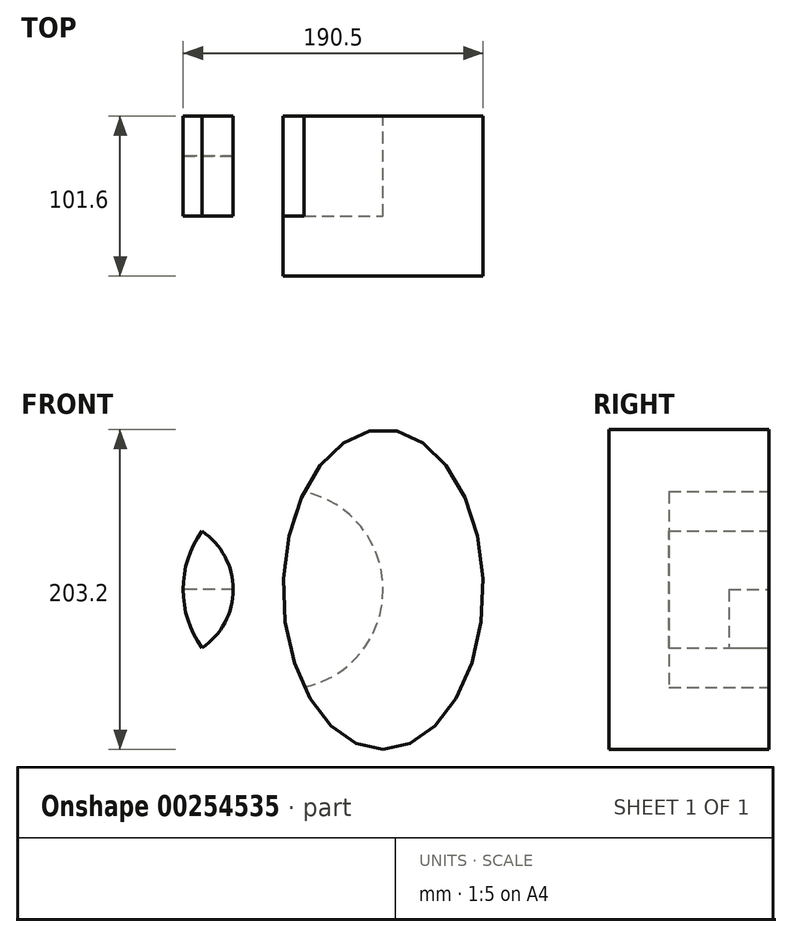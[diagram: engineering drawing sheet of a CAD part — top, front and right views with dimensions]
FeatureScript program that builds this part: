
annotation { "Feature Type Name" : "Feature", "Feature Type Description" : "" }
export const myFeature = defineFeature(function(context is Context, id is Id, definition is map)
    precondition{}
    {
        {
            var Q0;
            Q0=qCreatedBy(makeId("Front.planeOp"),FACE);
            var sketch = newSketch(context, id + "F0", { "sketchPlane" : qUnion([Q0])});
            skLineSegment(sketch, "E0", {"start": v(0, 0) * mm, "end": v(-76.2, 0) * mm});
            skCircle(sketch, "E1", {"center": v(-76.2, 0) * mm, "radius": 44.45 * mm});
            skLineSegment(sketch, "E2", {"start": v(-31.75, 0) * mm, "end": v(-63.5, 0) * mm});
            skCircle(sketch, "E3", {"center": v(0, 0) * mm, "radius": 63.5 * mm});
            skLineSegment(sketch, "E4", {"start": v(63.5, 0) * mm, "end": v(63.5, 101.6) * mm});
            skEllipse(sketch, "E5", {"center": v(63.5, 0) * mm, "majorRadius": 63.5 * mm, "minorRadius": 101.6 * mm, "majorAxis": v(-1, 0)});
            skSolve(sketch);
        }
        {
            var Q0;
            {var subQ0=sQuery(id+"F0.wireOp",EDGE,"E3");var subQ1=sQuery(id+"F0.wireOp",EDGE,"E1");var subQ2=makeQuery(id+"F0.imprint","INTERSECT",VERTEX,{"disambiguationData":[OD(0.0)],"derivedFrom":[subQ1,subQ0]});Q0=makeQuery(id+"F0.imprint","IMPRINT",FACE,{"disambiguationData":[TD([[makeQuery(id+"F0.imprint","IMPRINT",EDGE,{"disambiguationData":[TD([[subQ2,-1.0]])],"derivedFrom":subQ1}),1.0]])]});}
            extrude(context, id + "F1", {"entities" : qUnion([Q0]), "depth" : 25.4 * mm});
        }
        {
            var Q0;
            {var subQ3=sQuery(id+"F0.wireOp",EDGE,"E1");var subQ5=sQuery(id+"F0.wireOp",EDGE,"E3");var subQ6=makeQuery(id+"F0.imprint","INTERSECT",VERTEX,{"disambiguationData":[OD(0.0)],"derivedFrom":[subQ3,subQ5]});Q0=makeQuery(id+"F0.imprint","IMPRINT",FACE,{"disambiguationData":[TD([[makeQuery(id+"F0.imprint","IMPRINT",EDGE,{"disambiguationData":[TD([[subQ6,1.0]])],"derivedFrom":subQ5}),1.0]])]});}
            var Q1;
            {var subQ0=sQuery(id+"F0.wireOp",EDGE,"E2");Q1=makeQuery(id+"F0.imprint","IMPRINT",FACE,{"disambiguationData":[TD([[makeQuery(id+"F0.imprint","IMPRINT",EDGE,{"derivedFrom":subQ0}),-1.0]])]});}
            var Q2;
            {var subQ3=sQuery(id+"F0.wireOp",EDGE,"E1");var subQ5=sQuery(id+"F0.wireOp",EDGE,"E3");var subQ6=makeQuery(id+"F0.imprint","INTERSECT",VERTEX,{"disambiguationData":[OD(1.0)],"derivedFrom":[subQ3,subQ5]});Q2=makeQuery(id+"F0.imprint","IMPRINT",FACE,{"disambiguationData":[TD([[makeQuery(id+"F0.imprint","IMPRINT",EDGE,{"disambiguationData":[TD([[subQ6,-1.0]])],"derivedFrom":subQ5}),1.0]])]});}
            var Q3;
            {var subQ0=sQuery(id+"F0.wireOp",EDGE,"E3");var subQ1=makeQuery(id+"F0.imprint","INTERSECT",VERTEX,{"derivedFrom":[subQ0,sQuery(id+"F0.wireOp",EDGE,"E4")]});Q3=makeQuery(id+"F0.imprint","IMPRINT",FACE,{"disambiguationData":[TD([[makeQuery(id+"F0.imprint","IMPRINT",EDGE,{"disambiguationData":[TD([[subQ1,-1.0]])],"derivedFrom":subQ0}),1.0]])]});}
            var Q4;
            {var subQ0=sQuery(id+"F0.wireOp",EDGE,"E2");Q4=makeQuery(id+"F0.imprint","IMPRINT",FACE,{"disambiguationData":[TD([[makeQuery(id+"F0.imprint","IMPRINT",EDGE,{"derivedFrom":subQ0}),1.0]])]});}
            extrude(context, id + "F2", {"entities" : qUnion([Q0, Q1, Q2, Q3, Q4]), "depth" : 63.5 * mm});
        }
        {
            var Q0;
            {var subQ0=sQuery(id+"F0.wireOp",EDGE,"E4");Q0=makeQuery(id+"F0.imprint","IMPRINT",FACE,{"disambiguationData":[TD([[makeQuery(id+"F0.imprint","IMPRINT",EDGE,{"derivedFrom":subQ0}),1.0]])]});}
            var Q1;
            {var subQ0=sQuery(id+"F0.wireOp",EDGE,"E3");var subQ1=makeQuery(id+"F0.imprint","INTERSECT",VERTEX,{"derivedFrom":[subQ0,sQuery(id+"F0.wireOp",EDGE,"E4")]});Q1=makeQuery(id+"F0.imprint","IMPRINT",FACE,{"disambiguationData":[TD([[makeQuery(id+"F0.imprint","IMPRINT",EDGE,{"disambiguationData":[TD([[subQ1,-1.0]])],"derivedFrom":subQ0}),1.0]])]});}
            var Q2;
            {var subQ0=sQuery(id+"F0.wireOp",EDGE,"E4");Q2=makeQuery(id+"F0.imprint","IMPRINT",FACE,{"disambiguationData":[TD([[makeQuery(id+"F0.imprint","IMPRINT",EDGE,{"derivedFrom":subQ0}),-1.0]])]});}
            extrude(context, id + "F3", {"entities" : qUnion([Q0, Q1, Q2]), "depth" : 101.6 * mm});
        }
    });
